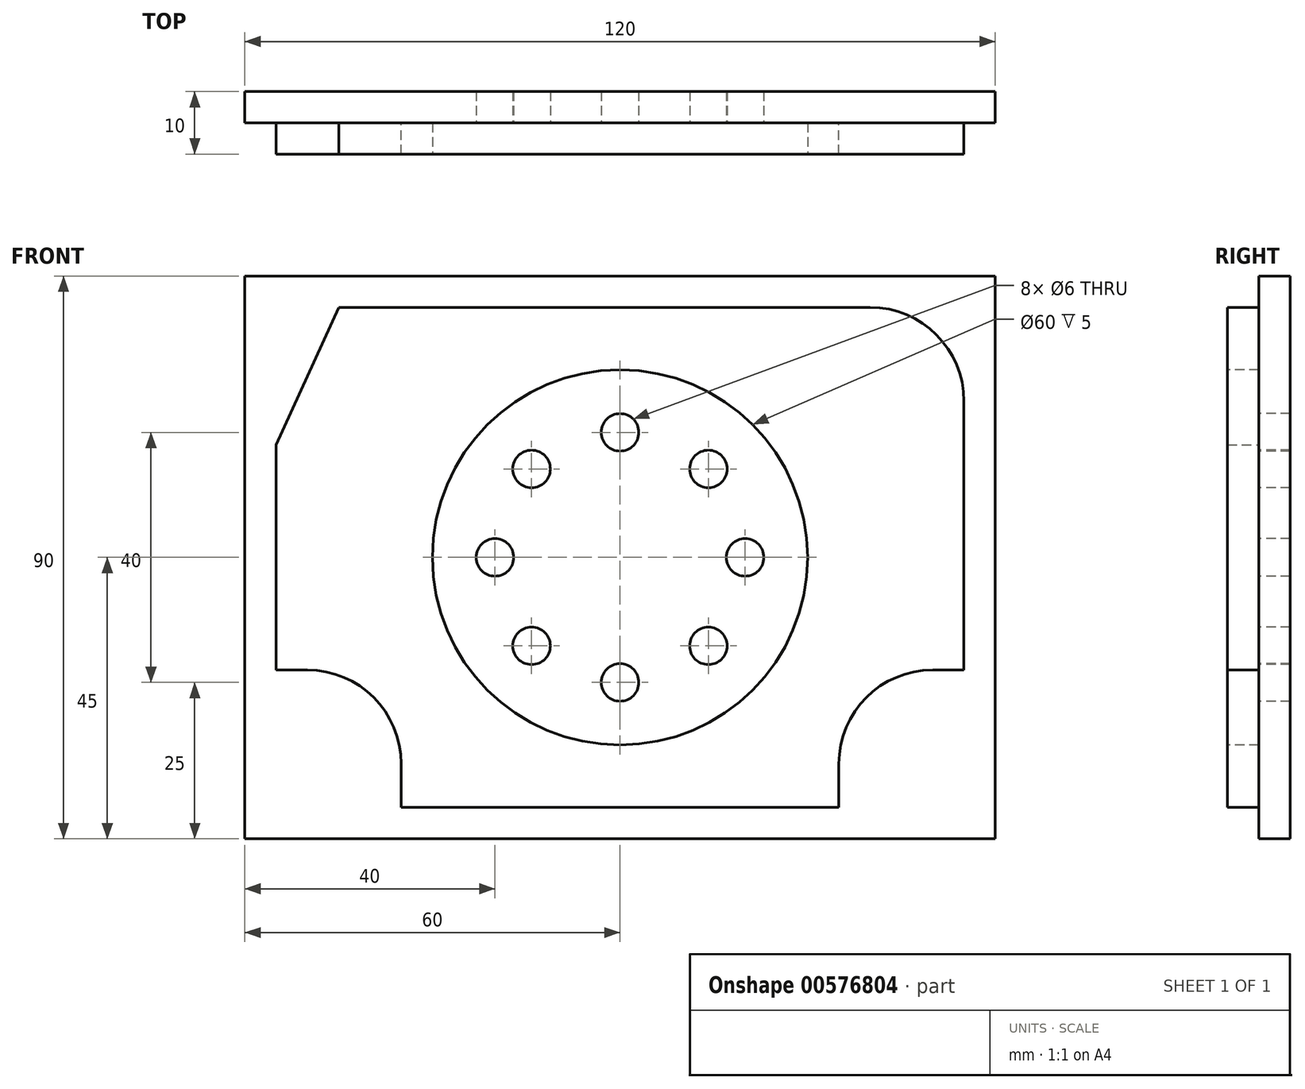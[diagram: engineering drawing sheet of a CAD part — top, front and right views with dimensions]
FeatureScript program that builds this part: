
annotation { "Feature Type Name" : "Feature", "Feature Type Description" : "" }
export const myFeature = defineFeature(function(context is Context, id is Id, definition is map)
    precondition{}
    {
        {
            var Q0;
            Q0=qCreatedBy(makeId("Front.planeOp"),FACE);
            var sketch = newSketch(context, id + "F0", { "sketchPlane" : qUnion([Q0])});
            skLineSegment(sketch, "E0", {"start": v(0, 0) * mm, "end": v(-120, 0) * mm});
            skLineSegment(sketch, "E1", {"start": v(-120, 0) * mm, "end": v(-120, 90) * mm});
            skLineSegment(sketch, "E2", {"start": v(0, 0) * mm, "end": v(0, 90) * mm});
            skLineSegment(sketch, "E3", {"start": v(-120, 90) * mm, "end": v(0, 90) * mm});
            skSolve(sketch);
        }
        {
            var Q0;
            Q0 = qSketchRegion(id + "F0", true);
            extrude(context, id + "F1", {"entities" : qUnion([Q0]), "depth" : 5 * mm, "offsetDistance" : 25 * mm});
        }
        {
            var Q0;
            Q0=makeQuery(id+"F1.opExtrude","CAP_FACE",FACE,{"disambiguationData":[OSD([sQuery(id+"F0.wireOp",EDGE,"E0"),sQuery(id+"F0.wireOp",EDGE,"E1"),sQuery(id+"F0.wireOp",EDGE,"E2"),sQuery(id+"F0.wireOp",EDGE,"E3")])],"isStart":false});
            var sketch = newSketch(context, id + "F2", { "sketchPlane" : qUnion([Q0])});
            skCircle(sketch, "E4", {"center": v(-60, 45) * mm, "radius": 20 * mm, "construction": true});
            skCircle(sketch, "E5", {"center": v(-60, 25) * mm, "radius": 3 * mm});
            skCircle(sketch, "E6", {"center": v(-80, 45) * mm, "radius": 3 * mm});
            skCircle(sketch, "E7", {"center": v(-40, 45) * mm, "radius": 3 * mm});
            skCircle(sketch, "E8", {"center": v(-60, 65) * mm, "radius": 3 * mm});
            skCircle(sketch, "E9", {"center": v(-45.86, 59.14) * mm, "radius": 3 * mm});
            skCircle(sketch, "E10", {"center": v(-74.14, 59.14) * mm, "radius": 3 * mm});
            skCircle(sketch, "E11", {"center": v(-45.86, 30.86) * mm, "radius": 3 * mm});
            skCircle(sketch, "E12", {"center": v(-74.14, 30.86) * mm, "radius": 3 * mm});
            skSolve(sketch);
        }
        {
            var Q0;
            Q0=sQuery(id+"F2.wireOp",VERTEX,"E8.center");
            var Q1;
            Q1=sQuery(id+"F2.wireOp",VERTEX,"E10.center");
            var Q2;
            Q2=sQuery(id+"F2.wireOp",VERTEX,"E6.center");
            var Q3;
            Q3=sQuery(id+"F2.wireOp",VERTEX,"E12.center");
            var Q4;
            Q4=sQuery(id+"F2.wireOp",VERTEX,"E5.center");
            var Q5;
            Q5=sQuery(id+"F2.wireOp",VERTEX,"E11.center");
            var Q6;
            Q6=sQuery(id+"F2.wireOp",VERTEX,"E7.center");
            var Q7;
            Q7=sQuery(id+"F2.wireOp",VERTEX,"E9.center");
            var Q8;
            Q8=makeQuery(id+"F1.opExtrude","SWEPT_BODY",BODY,{"disambiguationData":[OSD([sQuery(id+"F0.wireOp",EDGE,"E0"),sQuery(id+"F0.wireOp",EDGE,"E1"),sQuery(id+"F0.wireOp",EDGE,"E2"),sQuery(id+"F0.wireOp",EDGE,"E3")])]});
            hole(context, id + "F3", {"style" : HoleStyle.SIMPLE, "endStyle" : HoleEndStyle.THROUGH, "holeDiameter" : 6 * mm, "isTappedThrough" : true, "tappedDepth" : 12 * mm, "tapClearance" : 3, "locations" : qUnion([Q0, Q1, Q2, Q3, Q4, Q5, Q6, Q7]), "scope" : qUnion([Q8])});
        }
        {
            var Q0;
            Q0=makeQuery(id+"F1.opExtrude","CAP_FACE",FACE,{"disambiguationData":[OSD([sQuery(id+"F0.wireOp",EDGE,"E0"),sQuery(id+"F0.wireOp",EDGE,"E1"),sQuery(id+"F0.wireOp",EDGE,"E2"),sQuery(id+"F0.wireOp",EDGE,"E3")])],"isStart":false});
            var sketch = newSketch(context, id + "F4", { "sketchPlane" : qUnion([Q0])});
            skLineSegment(sketch, "E13", {"start": v(0, 0) * mm, "end": v(-5, 0) * mm, "construction": true});
            skLineSegment(sketch, "E14", {"start": v(-5, 0) * mm, "end": v(-5, 5) * mm, "construction": true});
            skLineSegment(sketch, "E15", {"start": v(-5, 5) * mm, "end": v(-25, 5) * mm, "construction": true});
            skLineSegment(sketch, "E16", {"start": v(-25, 5) * mm, "end": v(-95, 5) * mm});
            skLineSegment(sketch, "E17", {"start": v(-5, 5) * mm, "end": v(-5, 27) * mm, "construction": true});
            skLineSegment(sketch, "E18", {"start": v(-5, 27) * mm, "end": v(-5, 70) * mm});
            skLineSegment(sketch, "E19", {"start": v(-20, 85) * mm, "end": v(-105, 85) * mm});
            skPoint(sketch, "E20.visualSharp", {"position": v(-5, 85) * mm});
            skArc(sketch, "E20.filletArc", {"start": v(-5, 70) * mm, "mid": v(-9.4, 80.6) * mm, "end": v(-20, 85) * mm});
            skLineSegment(sketch, "E21", {"start": v(-25, 5) * mm, "end": v(-25, 12) * mm});
            skLineSegment(sketch, "E22", {"start": v(-10, 27) * mm, "end": v(-5, 27) * mm});
            skPoint(sketch, "E23.visualSharp", {"position": v(-25, 27) * mm});
            skArc(sketch, "E23.filletArc", {"start": v(-10, 27) * mm, "mid": v(-20.6, 22.6) * mm, "end": v(-25, 12) * mm});
            skLineSegment(sketch, "E24", {"start": v(-95, 5) * mm, "end": v(-95, 12) * mm});
            skLineSegment(sketch, "E25", {"start": v(-110, 27) * mm, "end": v(-115, 27) * mm});
            skPoint(sketch, "E26.visualSharp", {"position": v(-95, 27) * mm});
            skArc(sketch, "E26.filletArc", {"start": v(-95, 12) * mm, "mid": v(-99.4, 22.6) * mm, "end": v(-110, 27) * mm});
            skLineSegment(sketch, "E27", {"start": v(-115, 27) * mm, "end": v(-115, 63) * mm});
            skLineSegment(sketch, "E28", {"start": v(-115, 63) * mm, "end": v(-105, 85) * mm});
            skSolve(sketch);
        }
        {
            var Q0;
            Q0 = qSketchRegion(id + "F4", true);
            extrude(context, id + "F5", {"entities" : qUnion([Q0]), "operationType" : NewBodyOperationType.ADD, "depth" : 5 * mm, "offsetDistance" : 25 * mm});
        }
        {
            var Q0;
            Q0=makeQuery(id+"F5.opExtrude","CAP_FACE",FACE,{"disambiguationData":[OSD([sQuery(id+"F4.wireOp",EDGE,"E16"),sQuery(id+"F4.wireOp",EDGE,"E18"),sQuery(id+"F4.wireOp",EDGE,"E19"),sQuery(id+"F4.wireOp",EDGE,"E20.filletArc"),sQuery(id+"F4.wireOp",EDGE,"E21"),sQuery(id+"F4.wireOp",EDGE,"E22"),sQuery(id+"F4.wireOp",EDGE,"E23.filletArc"),sQuery(id+"F4.wireOp",EDGE,"E24"),sQuery(id+"F4.wireOp",EDGE,"E25"),sQuery(id+"F4.wireOp",EDGE,"E26.filletArc"),sQuery(id+"F4.wireOp",EDGE,"E27"),sQuery(id+"F4.wireOp",EDGE,"E28")])],"isStart":false});
            var sketch = newSketch(context, id + "F6", { "sketchPlane" : qUnion([Q0])});
            skCircle(sketch, "E29", {"center": v(-60, 45) * mm, "radius": 30 * mm});
            skSolve(sketch);
        }
        {
            var Q0;
            Q0=makeQuery(id+"F6.imprint","IMPRINT",FACE,{"disambiguationData":[TD([[makeQuery(id+"F6.imprint","IMPRINT",EDGE,{"derivedFrom":sQuery(id+"F6.wireOp",EDGE,"E29")}),1.0]])]});
            extrude(context, id + "F7", {"entities" : qUnion([Q0]), "operationType" : NewBodyOperationType.REMOVE, "oppositeDirection" : true, "depth" : 5 * mm, "offsetDistance" : 25 * mm});
        }
    });
